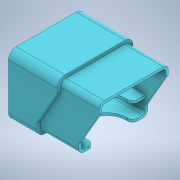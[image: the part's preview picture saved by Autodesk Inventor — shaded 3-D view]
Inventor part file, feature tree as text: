
AUTODESK INVENTOR PART (.ipt)
format: ipt  version: 2020 (Build 240168000, 168)  size: 337,408 bytes
history: native  units: in
note: dims shown in document units (in); Inventor stores cm internally (conversion verified against a paired STEP export)
features: extrude x7, fillet x5, sketch x3, other x2, chamfer x1, mirror x1
ambient origin geometry x8: Origin, YZ Plane, XZ Plane, XY Plane, X Axis, Y Axis, Z Axis, Center Point
bodies: Solid1 (feature_tree)
feature tree (19):
  other  "ESP32 Feather.ipt"
  sketch  "Sketch3"  dims[d1=0.3937in d2=0.0394in]
  extrude  "Extrusion1"  Depth=0.0394in
  extrude  "Extrusion2"  Depth=0.0394in
  extrude  "Extrusion3"  Depth=0.0787in
  fillet  "Fillet1"  Radius=0.1969in
  fillet  "Fillet2"  Radius=0.1969in
  fillet  "Fillet3"  Radius=0.2067in
  sketch  "Sketch4"  dims[d3=0.0591in d4=0.0394in]
  extrude  "Extrusion4"  Depth=0.9843in
  extrude  "Extrusion5"  Depth=0.0787in
  extrude  "Extrusion6"  Depth=0.0394in
  chamfer  "Chamfer1"  Distance=0.0394in
  fillet  "Fillet6"  Radius=0.0394in
  extrude  "Extrusion8"  Depth=0.0787in
  fillet  "Fillet7"  Radius=0.0098in
  mirror  "Mirror2"
  other  "ESP32 Feather"
  sketch  "Sketch6"  dims[d7=0.0394in d8=0.0197in d9=0.0098in d13=0.1969in d14=0.1969in d17=0.2067in d18=0.9843in d19=0.5118in d21=0.0394in d22=0.0394in d23=0.0394in d24=0.0098in d25=0.0098in d26=0.0098in d27=0.0098in d28=0.0098in d29=0.0098in d30=0.5906in d32=30.0deg d33=0.5906in d35=0.0098in d36=0.1969in d37=0.1969in d38=0.4872in d39=0.0in d40=0.0886in d41=0.0in d42=0.0394in d43=0.0in d44=0.0394in d45=0.0787in d46=0.1181in d50=45.0deg d52=0.1969in d53=0.0591in d54=45.0deg d55=0.0394in d56=0.0394in d57=0.0in d58=0.0354in d59=0.0in d60=0.0689in d61=0.0in d62=0.0354in d63=0.0591in d64=45.0deg d65=0.0591in d66=0.0394in d67=1.4567in d70=0.1969in d71=0.0984in d72=45.0deg d80=0.3937in d81=0.2953in d82=0.3937in d83=0.0in d84=0.0787in]
